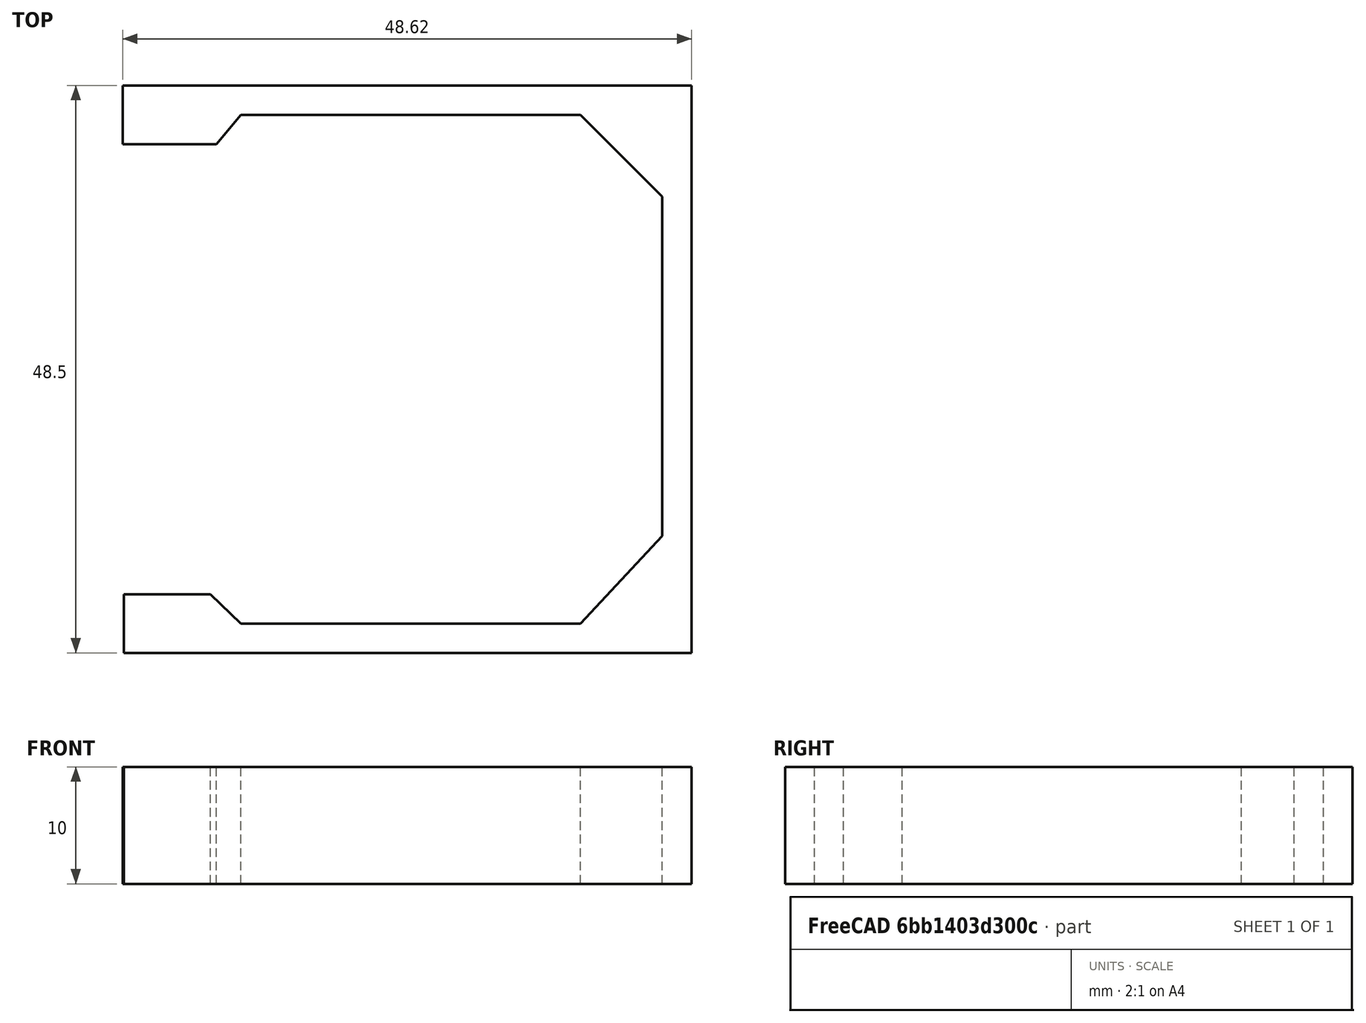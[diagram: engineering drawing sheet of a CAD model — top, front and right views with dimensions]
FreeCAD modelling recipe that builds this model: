
FCSTD DOCUMENT  (FreeCAD 1.2R20260113 (Git shallow))
Label: ender 3 revised kusba mount
License: All rights reserved
LicenseURL: http://en.wikipedia.org/wiki/All_rights_reserved
objects: App::Point×1, Sketcher::SketchObject×1, PartDesign::Pad×1, PartDesign::Body×1
note: 6 computed .brp shape members not serialized (recipe doc carries the construction recipe); baked Part::Feature solids carry a one-line shape summary decoded from their .brp

FEATURE [App::Point] Origin001
  Role = Origin
FEATURE [Sketcher::SketchObject] Sketch
  ArcFitTolerance = 1e-06
  AttachmentSupport = -> [Origin]
  ExternalTypes = [0]
  FullyConstrained = false
  MakeInternals = false
  MapMode = 5
  sketch-geometry (14):
    g0: LineSegment StartX=-8.9599 StartY=21.1467 StartZ=0 EndX=20.0401 EndY=21.1467 EndZ=0
    g1: LineSegment StartX=-8.9599 StartY=-22.3533 StartZ=0 EndX=20.0401 EndY=-22.3533 EndZ=0
    g2: LineSegment StartX=27.0401 StartY=14.1467 StartZ=0 EndX=27.0401 EndY=-14.8533 EndZ=0
    g3: LineSegment StartX=-8.9599 StartY=21.1467 StartZ=0 EndX=-11.0575 EndY=18.6467 EndZ=0
    g4: LineSegment StartX=-8.9599 StartY=-22.3533 StartZ=0 EndX=-11.5756 EndY=-19.8533 EndZ=0
    g5: LineSegment StartX=20.0401 StartY=21.1467 StartZ=0 EndX=27.0401 EndY=14.1467 EndZ=0
    g6: LineSegment StartX=27.0401 StartY=-14.8533 StartZ=0 EndX=20.0401 EndY=-22.3533 EndZ=0
    g7: LineSegment StartX=-19.0756 StartY=23.6467 StartZ=0 EndX=-19.0756 EndY=18.6467 EndZ=0
    g8: LineSegment StartX=-18.977 StartY=-24.8533 StartZ=0 EndX=29.5401 EndY=-24.8533 EndZ=0
    g9: LineSegment StartX=29.5401 StartY=-24.8533 StartZ=0 EndX=29.5401 EndY=23.6467 EndZ=0
    g10: LineSegment StartX=29.5401 StartY=23.6467 StartZ=0 EndX=-19.0756 EndY=23.6467 EndZ=0
    g11: LineSegment StartX=-18.977 StartY=-19.8533 StartZ=0 EndX=-18.977 EndY=-24.8533 EndZ=0
    g12: LineSegment StartX=-19.0756 StartY=18.6467 StartZ=0 EndX=-11.0575 EndY=18.6467 EndZ=0
    g13: LineSegment StartX=-18.977 StartY=-19.8533 StartZ=0 EndX=-11.5756 EndY=-19.8533 EndZ=0
  constraints (36):
    c: Horizontal(g0)
    c: Horizontal(g1)
    c: Vertical(g2)
    c: Equal(g0,g2)
    c: Equal(g2,g1)
    c: DistanceX(g0,g0) = 29
    c: DistanceX(g0,g2) = 7
    c: DistanceY(g2,g0) = 7
    c: Vertical(g0,g1)
    c: DistanceY(g1,g2) = 7.5
    c: Coincident(g3,g0)
    c: Coincident(g4,g1)
    c: Coincident(g5,g0)
    c: Coincident(g5,g2)
    c: Coincident(g6,g2)
    c: Coincident(g6,g1)
    c: Coincident(g11,g8)
    c: Coincident(g8,g9)
    c: Coincident(g9,g10)
    c: Coincident(g10,g7)
    c: Vertical(g9)
    c: Horizontal(g8)
    c: Horizontal(g10)
    c: DistanceY(g8,g1) = 2.5
    c: DistanceY(g0,g9) = 2.5
    c: DistanceX(g2,g9) = 2.5
    c: Horizontal(g12)
    c: Horizontal(g13)
    c: DistanceY(g8,g13) = 5
    c: Distance(g7,g12) = 5
    c: Coincident(g12,g3)
    c: Vertical(g7)
    c: Coincident(g12,g7)
    c: Coincident(g13,g4)
    c: Vertical(g11)
    c: Coincident(g11,g13)
FEATURE [PartDesign::Pad] Pad
  Direction = (0,0,1)
  Length = 10
  Length2 = 10
  Profile = -> Sketch
  ReferenceAxis = -> Sketch [N_Axis]
  SideType = 0
  Suppressed = false
  Type = 0
  Type2 = 0
FEATURE [PartDesign::Body] Body
  AllowCompound = false
  Group = -> [Sketch,Pad]
  Origin = -> Origin
  Tip = -> Pad
